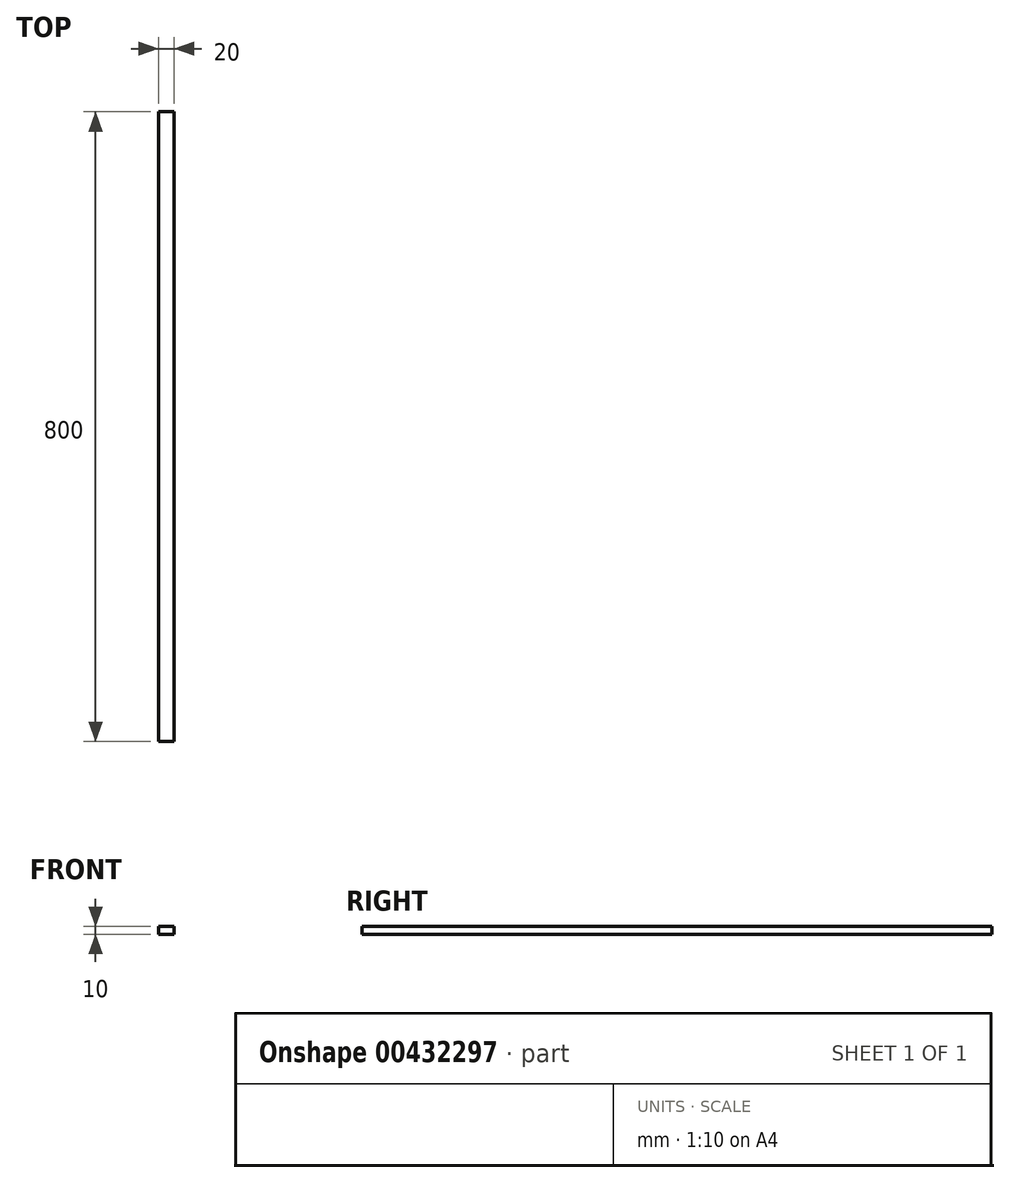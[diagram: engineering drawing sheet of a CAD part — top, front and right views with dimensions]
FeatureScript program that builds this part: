
annotation { "Feature Type Name" : "Feature", "Feature Type Description" : "" }
export const myFeature = defineFeature(function(context is Context, id is Id, definition is map)
    precondition{}
    {
        {
            var Q0;
            Q0=qCreatedBy(makeId("Top.planeOp"),FACE);
            var sketch = newSketch(context, id + "F0", { "sketchPlane" : qUnion([Q0])});
            skLineSegment(sketch, "E0.bottom", {"start": v(10, -400) * mm, "end": v(-10, -400) * mm});
            skLineSegment(sketch, "E0.top", {"start": v(10, 400) * mm, "end": v(-10, 400) * mm});
            skLineSegment(sketch, "E0.left", {"start": v(10, -400) * mm, "end": v(10, 400) * mm});
            skLineSegment(sketch, "E0.right", {"start": v(-10, -400) * mm, "end": v(-10, 400) * mm});
            skPoint(sketch, "E0.middle", {"position": v(0, 0) * mm});
            skSolve(sketch);
        }
        {
            var Q0;
            Q0=makeQuery(id+"F0.imprint","IMPRINT",FACE,{"disambiguationData":[TD([[makeQuery(id+"F0.imprint","IMPRINT",EDGE,{"derivedFrom":sQuery(id+"F0.wireOp",EDGE,"E0.bottom")}),-1.0]])]});
            extrude(context, id + "F1", {"entities" : qUnion([Q0]), "depth" : 10 * mm});
        }
    });
